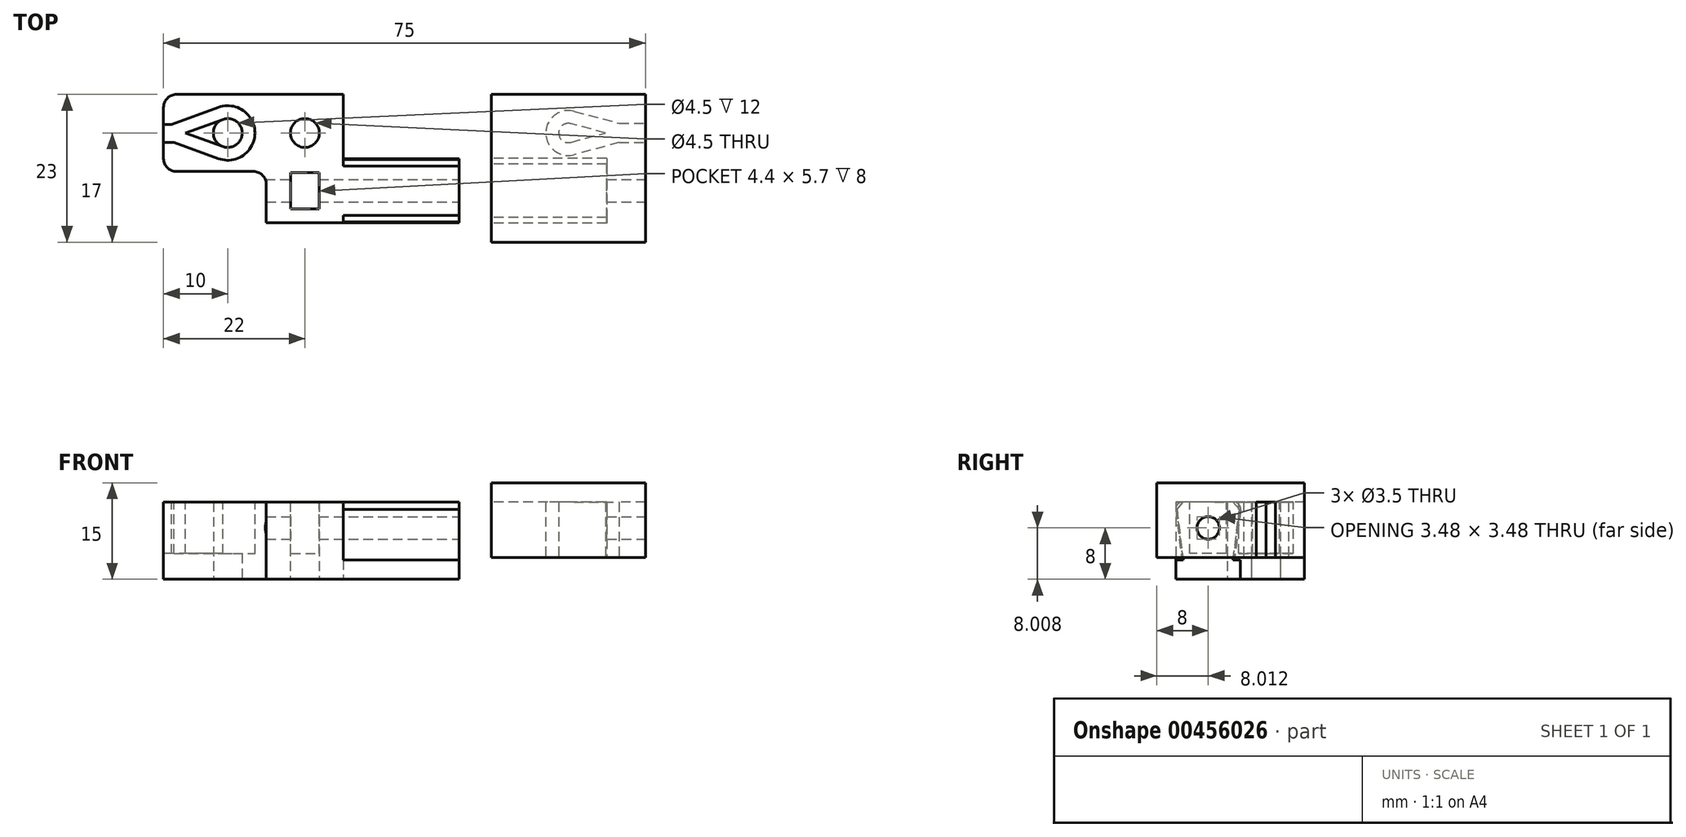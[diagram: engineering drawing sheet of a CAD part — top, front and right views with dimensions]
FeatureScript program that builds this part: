
annotation { "Feature Type Name" : "Feature", "Feature Type Description" : "" }
export const myFeature = defineFeature(function(context is Context, id is Id, definition is map)
    precondition{}
    {
        {
            var Q0;
            Q0=qCreatedBy(makeId("Top.planeOp"),FACE);
            var sketch = newSketch(context, id + "F0", { "sketchPlane" : qUnion([Q0])});
            skLineSegment(sketch, "E0.bottom", {"start": v(-8, -6) * mm, "end": v(4, -6) * mm});
            skLineSegment(sketch, "E0.top", {"start": v(-8, 6) * mm, "end": v(18, 6) * mm});
            skLineSegment(sketch, "E0.left", {"start": v(-10, -4) * mm, "end": v(-10, 4) * mm});
            skLineSegment(sketch, "E0.right", {"start": v(36, -6) * mm, "end": v(36, -4) * mm});
            skCircle(sketch, "E1", {"center": v(0, 0) * mm, "radius": 2.25 * mm, "construction": true});
            skPoint(sketch, "E2.visualSharp", {"position": v(-10, 6) * mm});
            skArc(sketch, "E2.filletArc", {"start": v(-8, 6) * mm, "mid": v(-9.41, 5.41) * mm, "end": v(-10, 4) * mm});
            skPoint(sketch, "E3.visualSharp", {"position": v(-10, -6) * mm});
            skArc(sketch, "E3.filletArc", {"start": v(-10, -4) * mm, "mid": v(-9.41, -5.41) * mm, "end": v(-8, -6) * mm});
            skCircle(sketch, "E4", {"center": v(12, 0) * mm, "radius": 2.25 * mm, "construction": true});
            skLineSegment(sketch, "E5", {"start": v(6, -8) * mm, "end": v(6, -14) * mm});
            skLineSegment(sketch, "E6", {"start": v(6, -14) * mm, "end": v(36, -14) * mm});
            skLineSegment(sketch, "E7", {"start": v(36, -6) * mm, "end": v(36, -14) * mm});
            skPoint(sketch, "E8.visualSharp", {"position": v(6, -6) * mm});
            skArc(sketch, "E8.filletArc", {"start": v(6, -8) * mm, "mid": v(5.41, -6.59) * mm, "end": v(4, -6) * mm});
            skLineSegment(sketch, "E9", {"start": v(18, 6) * mm, "end": v(18, -4) * mm});
            skLineSegment(sketch, "E10", {"start": v(18, -4) * mm, "end": v(36, -4) * mm});
            skSolve(sketch);
        }
        {
            var Q0;
            Q0 = qSketchRegion(id + "F0", true);
            extrude(context, id + "F1", {"entities" : qUnion([Q0]), "depth" : 12 * mm});
        }
        {
            var Q0;
            Q0=makeQuery(id+"F1.opExtrude","SWEPT_FACE",FACE,{"disambiguationData":[OSD([sQuery(id+"F0.wireOp",EDGE,"E0.right"),sQuery(id+"F0.wireOp",EDGE,"E7")])]});
            var sketch = newSketch(context, id + "F2", { "sketchPlane" : qUnion([Q0])});
            skLineSegment(sketch, "E11", {"start": v(-14, 12) * mm, "end": v(-12.9, 3) * mm});
            skLineSegment(sketch, "E12", {"start": v(-12.9, 3) * mm, "end": v(-16, 3) * mm});
            skLineSegment(sketch, "E13", {"start": v(-16, 3) * mm, "end": v(-16, 12) * mm});
            skLineSegment(sketch, "E14", {"start": v(-16, 12) * mm, "end": v(-14, 12) * mm});
            skPoint(sketch, "E15", {"position": v(-9, 0) * mm});
            skLineSegment(sketch, "E16", {"start": v(-9, -1.64) * mm, "end": v(-9, 13.82) * mm, "construction": true});
            skLineSegment(sketch, "E17.MirrorCS", {"start": v(-2, 12) * mm, "end": v(-4, 12) * mm});
            skLineSegment(sketch, "E18.MirrorCS", {"start": v(-2, 3) * mm, "end": v(-2, 12) * mm});
            skLineSegment(sketch, "E19.MirrorCS", {"start": v(-4, 12) * mm, "end": v(-5.1, 3) * mm});
            skLineSegment(sketch, "E20.MirrorCS", {"start": v(-5.1, 3) * mm, "end": v(-2, 3) * mm});
            skSolve(sketch);
        }
        {
            var Q0;
            Q0 = qSketchRegion(id + "F2", true);
            var Q1;
            Q1=makeQuery(id+"F1.opExtrude","SWEPT_FACE",FACE,{"disambiguationData":[OSD([sQuery(id+"F0.wireOp",EDGE,"E9")])]});
            extrude(context, id + "F3", {"entities" : qUnion([Q0]), "operationType" : NewBodyOperationType.REMOVE, "endBound" : BoundingType.UP_TO_SURFACE, "oppositeDirection" : true, "endBoundEntityFace" : qUnion([Q1]), "depth" : 25 * mm});
        }
        {
            var Q0;
            {var subQ0=sQuery(id+"F0.wireOp",EDGE,"E6");Q0=makeQuery(id+"F3.boolean.opBoolean","MERGE",EDGE,{"derivedFrom":[makeQuery(id+"F1.opExtrude","CAP_EDGE",EDGE,{"disambiguationData":[OSD([subQ0])],"isStart":false}),makeQuery(id+"F3.opExtrude","SWEPT_EDGE",EDGE,{"disambiguationData":[OSD([sQuery(id+"F0.wireOp",EDGE,"E0.right"),subQ0,sQuery(id+"F0.wireOp",EDGE,"E7"),sQuery(id+"F2.wireOp",EDGE,"E11"),sQuery(id+"F2.wireOp",EDGE,"E14")])]})]});}
            var Q1;
            {var subQ0=sQuery(id+"F0.wireOp",EDGE,"E10");Q1=makeQuery(id+"F3.boolean.opBoolean","MERGE",EDGE,{"derivedFrom":[makeQuery(id+"F1.opExtrude","CAP_EDGE",EDGE,{"disambiguationData":[OSD([subQ0])],"isStart":false}),makeQuery(id+"F3.opExtrude","SWEPT_EDGE",EDGE,{"disambiguationData":[OSD([sQuery(id+"F0.wireOp",EDGE,"E0.right"),sQuery(id+"F0.wireOp",EDGE,"E7"),subQ0,sQuery(id+"F2.wireOp",EDGE,"E17.MirrorCS"),sQuery(id+"F2.wireOp",EDGE,"E19.MirrorCS")])]})]});}
            chamfer(context, id + "F4", {"entities" : qUnion([Q0, Q1]), "width" : 1 * mm});
        }
        {
            var Q0;
            Q0=sQuery(id+"F0.wireOp",VERTEX,"E1.center");
            var Q1;
            Q1=sQuery(id+"F0.wireOp",VERTEX,"E4.center");
            var Q2;
            Q2=makeQuery(id+"F1.opExtrude","SWEPT_BODY",BODY,{"disambiguationData":[OSD([sQuery(id+"F0.wireOp",EDGE,"E0.bottom"),sQuery(id+"F0.wireOp",EDGE,"E0.top"),sQuery(id+"F0.wireOp",EDGE,"E0.left"),sQuery(id+"F0.wireOp",EDGE,"E0.right"),sQuery(id+"F0.wireOp",EDGE,"E2.filletArc"),sQuery(id+"F0.wireOp",EDGE,"E3.filletArc"),sQuery(id+"F0.wireOp",EDGE,"E5"),sQuery(id+"F0.wireOp",EDGE,"E6"),sQuery(id+"F0.wireOp",EDGE,"E7"),sQuery(id+"F0.wireOp",EDGE,"E8.filletArc"),sQuery(id+"F0.wireOp",EDGE,"E9"),sQuery(id+"F0.wireOp",EDGE,"E10")])]});
            hole(context, id + "F5", {"style" : HoleStyle.SIMPLE, "endStyle" : HoleEndStyle.THROUGH, "oppositeDirection" : true, "holeDiameter" : 4.5 * mm, "isTappedThrough" : true, "tappedDepth" : 12 * mm, "tapClearance" : 3, "startFromSketch" : true, "locations" : qUnion([Q0, Q1]), "scope" : qUnion([Q2])});
        }
        {
            var Q0;
            Q0=makeQuery(id+"F1.opExtrude","SWEPT_FACE",FACE,{"disambiguationData":[OSD([sQuery(id+"F0.wireOp",EDGE,"E0.right"),sQuery(id+"F0.wireOp",EDGE,"E7")])]});
            var sketch = newSketch(context, id + "F6", { "sketchPlane" : qUnion([Q0])});
            skPoint(sketch, "E21", {"position": v(-9, 0) * mm});
            skLineSegment(sketch, "E22", {"start": v(-9, -0.78) * mm, "end": v(-9, 13.1) * mm, "construction": true});
            skCircle(sketch, "E23", {"center": v(-9, 8) * mm, "radius": 1.75 * mm});
            skSolve(sketch);
        }
        {
            var Q0;
            Q0 = qSketchRegion(id + "F6", true);
            extrude(context, id + "F7", {"entities" : qUnion([Q0]), "operationType" : NewBodyOperationType.REMOVE, "oppositeDirection" : true, "depth" : 35 * mm});
        }
        {
            var Q0;
            Q0=makeQuery(id+"F1.opExtrude","CAP_FACE",FACE,{"disambiguationData":[OSD([sQuery(id+"F0.wireOp",EDGE,"E0.bottom"),sQuery(id+"F0.wireOp",EDGE,"E0.top"),sQuery(id+"F0.wireOp",EDGE,"E0.left"),sQuery(id+"F0.wireOp",EDGE,"E0.right"),sQuery(id+"F0.wireOp",EDGE,"E2.filletArc"),sQuery(id+"F0.wireOp",EDGE,"E3.filletArc"),sQuery(id+"F0.wireOp",EDGE,"E5"),sQuery(id+"F0.wireOp",EDGE,"E6"),sQuery(id+"F0.wireOp",EDGE,"E7"),sQuery(id+"F0.wireOp",EDGE,"E8.filletArc"),sQuery(id+"F0.wireOp",EDGE,"E9"),sQuery(id+"F0.wireOp",EDGE,"E10")])],"isStart":false});
            var sketch = newSketch(context, id + "F8", { "sketchPlane" : qUnion([Q0])});
            skLineSegment(sketch, "E24.bottom", {"start": v(9.8, -6.15) * mm, "end": v(14.2, -6.15) * mm});
            skLineSegment(sketch, "E24.top", {"start": v(9.8, -11.85) * mm, "end": v(14.2, -11.85) * mm});
            skLineSegment(sketch, "E24.left", {"start": v(9.8, -6.15) * mm, "end": v(9.8, -11.85) * mm});
            skLineSegment(sketch, "E24.right", {"start": v(14.2, -6.15) * mm, "end": v(14.2, -11.85) * mm});
            skPoint(sketch, "E25", {"position": v(14.2, -9) * mm});
            skPoint(sketch, "E26", {"position": v(12, -6.15) * mm});
            skLineSegment(sketch, "E27", {"start": v(12, 0) * mm, "end": v(12, -15.07) * mm, "construction": true});
            skPoint(sketch, "E28", {"position": v(36, -9) * mm});
            skLineSegment(sketch, "E29", {"start": v(36, -9) * mm, "end": v(2.23, -9) * mm, "construction": true});
            skSolve(sketch);
        }
        {
            var Q0;
            Q0 = qSketchRegion(id + "F8", true);
            extrude(context, id + "F9", {"entities" : qUnion([Q0]), "operationType" : NewBodyOperationType.REMOVE, "oppositeDirection" : true, "depth" : 8 * mm});
        }
        {
            var Q0;
            Q0=makeQuery(id+"F1.opExtrude","CAP_FACE",FACE,{"disambiguationData":[OSD([sQuery(id+"F0.wireOp",EDGE,"E0.bottom"),sQuery(id+"F0.wireOp",EDGE,"E0.top"),sQuery(id+"F0.wireOp",EDGE,"E0.left"),sQuery(id+"F0.wireOp",EDGE,"E0.right"),sQuery(id+"F0.wireOp",EDGE,"E2.filletArc"),sQuery(id+"F0.wireOp",EDGE,"E3.filletArc"),sQuery(id+"F0.wireOp",EDGE,"E5"),sQuery(id+"F0.wireOp",EDGE,"E6"),sQuery(id+"F0.wireOp",EDGE,"E7"),sQuery(id+"F0.wireOp",EDGE,"E8.filletArc"),sQuery(id+"F0.wireOp",EDGE,"E9"),sQuery(id+"F0.wireOp",EDGE,"E10")])],"isStart":false});
            var sketch = newSketch(context, id + "F10", { "sketchPlane" : qUnion([Q0])});
            skLineSegment(sketch, "E30", {"start": v(-0.77, 2.11) * mm, "end": v(-6.58, 0) * mm});
            skLineSegment(sketch, "E31", {"start": v(-6.58, 0) * mm, "end": v(-0.77, -2.11) * mm});
            skArc(sketch, "E32.0", {"start": v(-0.77, -2.11) * mm, "mid": v(2.25, 0) * mm, "end": v(-0.77, 2.11) * mm});
            skLineSegment(sketch, "E33", {"start": v(0, 0) * mm, "end": v(-11.05, 0) * mm, "construction": true});
            skPoint(sketch, "E33.endSnap0", {"position": v(-10, 0) * mm});
            skLineSegment(sketch, "E34.0", {"start": v(-8.4, -1.47) * mm, "end": v(-1.47, -3.99) * mm});
            skLineSegment(sketch, "E35.0", {"start": v(-1.47, 3.99) * mm, "end": v(-8.76, 1.33) * mm});
            skLineSegment(sketch, "E36", {"start": v(-10.71, 1.33) * mm, "end": v(-10.71, -1.47) * mm});
            skLineSegment(sketch, "E37.trimOffspring", {"start": v(-8.76, 1.33) * mm, "end": v(-10.71, 1.33) * mm});
            skLineSegment(sketch, "E38.trimOffspring", {"start": v(-8.4, -1.47) * mm, "end": v(-10.71, -1.47) * mm});
            skArc(sketch, "E39.trimOffspring", {"start": v(-1.47, -3.99) * mm, "mid": v(4.23, 0) * mm, "end": v(-1.47, 3.99) * mm});
            skSolve(sketch);
        }
        {
            var Q0;
            Q0 = qSketchRegion(id + "F10", true);
            extrude(context, id + "F11", {"entities" : qUnion([Q0]), "operationType" : NewBodyOperationType.REMOVE, "oppositeDirection" : true, "depth" : 8 * mm});
        }
        {
            var Q0;
            Q0=makeQuery(id+"F6.imprint","IMPRINT",FACE,{"disambiguationData":[TD([[makeQuery(id+"F6.imprint","IMPRINT",EDGE,{"derivedFrom":sQuery(id+"F6.wireOp",EDGE,"E23")}),-1.0]])]});
            cPlane(context, id + "F12", {"entities" : qUnion([Q0]), "cplaneType" : CPlaneType.OFFSET, "offset" : 5 * mm, "width" : 150 * mm, "height" : 150 * mm});
        }
        {
            var Q0;
            Q0=qCreatedBy(id+"F12.planeOp",FACE);
            var sketch = newSketch(context, id + "F13", { "sketchPlane" : qUnion([Q0])});
            skLineSegment(sketch, "E40.0", {"start": v(-14.06, 10.8) * mm, "end": v(-13.15, 3.4) * mm});
            skLineSegment(sketch, "E41.0", {"start": v(-3.94, 10.8) * mm, "end": v(-4.85, 3.4) * mm});
            skLineSegment(sketch, "E42.0", {"start": v(-13.15, 3.4) * mm, "end": v(-14, 3.4) * mm});
            skLineSegment(sketch, "E43.0", {"start": v(-4.85, 3.4) * mm, "end": v(-4, 3.4) * mm});
            skLineSegment(sketch, "E44", {"start": v(-14, 3.4) * mm, "end": v(-17, 3.4) * mm});
            skLineSegment(sketch, "E45", {"start": v(-17, 3.4) * mm, "end": v(-17, 15) * mm});
            skLineSegment(sketch, "E46", {"start": v(-17, 15) * mm, "end": v(6, 15) * mm});
            skLineSegment(sketch, "E47", {"start": v(6, 15) * mm, "end": v(6, 3.4) * mm});
            skLineSegment(sketch, "E48", {"start": v(6, 3.4) * mm, "end": v(-4, 3.4) * mm});
            skLineSegment(sketch, "E49.0", {"start": v(-5, 12) * mm, "end": v(-13, 12) * mm});
            skArc(sketch, "E50", {"start": v(-13, 12) * mm, "mid": v(-13.8, 11.64) * mm, "end": v(-14.06, 10.8) * mm});
            skArc(sketch, "E51", {"start": v(-3.94, 10.8) * mm, "mid": v(-4.2, 11.64) * mm, "end": v(-5, 12) * mm});
            skPoint(sketch, "E52.orphan", {"position": v(-13, 12) * mm});
            skPoint(sketch, "E53.orphan", {"position": v(-5, 12) * mm});
            skSolve(sketch);
        }
        {
            var Q0;
            Q0 = qSketchRegion(id + "F13", true);
            extrude(context, id + "F14", {"entities" : qUnion([Q0]), "depth" : 24 * mm});
        }
        {
            var Q0;
            Q0=makeQuery(id+"F14.opExtrude","CAP_FACE",FACE,{"disambiguationData":[OSD([sQuery(id+"F13.wireOp",EDGE,"E40.0"),sQuery(id+"F13.wireOp",EDGE,"E41.0"),sQuery(id+"F13.wireOp",EDGE,"E42.0"),sQuery(id+"F13.wireOp",EDGE,"E43.0"),sQuery(id+"F13.wireOp",EDGE,"E44"),sQuery(id+"F13.wireOp",EDGE,"E45"),sQuery(id+"F13.wireOp",EDGE,"E46"),sQuery(id+"F13.wireOp",EDGE,"E47"),sQuery(id+"F13.wireOp",EDGE,"E48"),sQuery(id+"F13.wireOp",EDGE,"E49.0"),sQuery(id+"F13.wireOp",EDGE,"E50"),sQuery(id+"F13.wireOp",EDGE,"E51")])],"isStart":false});
            var sketch = newSketch(context, id + "F15", { "sketchPlane" : qUnion([Q0])});
            skLineSegment(sketch, "E54.bottom", {"start": v(-17, 15) * mm, "end": v(-3, 15) * mm});
            skLineSegment(sketch, "E54.top", {"start": v(-17, 3.4) * mm, "end": v(-3, 3.4) * mm});
            skLineSegment(sketch, "E54.left", {"start": v(-17, 15) * mm, "end": v(-17, 3.4) * mm});
            skLineSegment(sketch, "E54.right", {"start": v(-3, 15) * mm, "end": v(-3, 3.4) * mm});
            skSolve(sketch);
        }
        {
            var Q0;
            Q0 = qSketchRegion(id + "F15", true);
            extrude(context, id + "F16", {"entities" : qUnion([Q0]), "operationType" : NewBodyOperationType.ADD, "oppositeDirection" : true, "depth" : 6 * mm});
        }
        {
            var Q0;
            Q0=makeQuery(id+"F16.boolean.opBoolean","MERGE",FACE,{"derivedFrom":[makeQuery(id+"F14.opExtrude","CAP_FACE",FACE,{"disambiguationData":[OSD([sQuery(id+"F13.wireOp",EDGE,"E40.0"),sQuery(id+"F13.wireOp",EDGE,"E41.0"),sQuery(id+"F13.wireOp",EDGE,"E42.0"),sQuery(id+"F13.wireOp",EDGE,"E43.0"),sQuery(id+"F13.wireOp",EDGE,"E44"),sQuery(id+"F13.wireOp",EDGE,"E45"),sQuery(id+"F13.wireOp",EDGE,"E46"),sQuery(id+"F13.wireOp",EDGE,"E47"),sQuery(id+"F13.wireOp",EDGE,"E48"),sQuery(id+"F13.wireOp",EDGE,"E49.0"),sQuery(id+"F13.wireOp",EDGE,"E50"),sQuery(id+"F13.wireOp",EDGE,"E51")])],"isStart":false}),makeQuery(id+"F16.opExtrude","CAP_FACE",FACE,{"disambiguationData":[OSD([sQuery(id+"F15.wireOp",EDGE,"E54.bottom"),sQuery(id+"F15.wireOp",EDGE,"E54.top"),sQuery(id+"F15.wireOp",EDGE,"E54.left"),sQuery(id+"F15.wireOp",EDGE,"E54.right")])],"isStart":true})]});
            var sketch = newSketch(context, id + "F17", { "sketchPlane" : qUnion([Q0])});
            skCircle(sketch, "E55.0", {"center": v(-9, 8) * mm, "radius": 1.75 * mm});
            skSolve(sketch);
        }
        {
            var Q0;
            Q0 = qSketchRegion(id + "F17", true);
            var Q1;
            Q1=makeQuery(id+"F16.opExtrude","CAP_FACE",FACE,{"disambiguationData":[OSD([sQuery(id+"F15.wireOp",EDGE,"E54.bottom"),sQuery(id+"F15.wireOp",EDGE,"E54.top"),sQuery(id+"F15.wireOp",EDGE,"E54.left"),sQuery(id+"F15.wireOp",EDGE,"E54.right")])],"isStart":false});
            extrude(context, id + "F18", {"entities" : qUnion([Q0]), "operationType" : NewBodyOperationType.REMOVE, "endBound" : BoundingType.UP_TO_SURFACE, "oppositeDirection" : true, "endBoundEntityFace" : qUnion([Q1]), "depth" : 25 * mm});
        }
        {
            var Q0;
            Q0=makeQuery(id+"F16.boolean.opBoolean","MERGE",FACE,{"derivedFrom":[makeQuery(id+"F14.opExtrude","SWEPT_FACE",FACE,{"disambiguationData":[OSD([sQuery(id+"F13.wireOp",EDGE,"E42.0"),sQuery(id+"F13.wireOp",EDGE,"E44")])]}),makeQuery(id+"F14.opExtrude","SWEPT_FACE",FACE,{"disambiguationData":[OSD([sQuery(id+"F13.wireOp",EDGE,"E43.0"),sQuery(id+"F13.wireOp",EDGE,"E48")])]}),makeQuery(id+"F16.opExtrude","SWEPT_FACE",FACE,{"disambiguationData":[OSD([sQuery(id+"F15.wireOp",EDGE,"E54.top")])]})]});
            var sketch = newSketch(context, id + "F19", { "sketchPlane" : qUnion([Q0])});
            skArc(sketch, "E56", {"start": v(53.39, 1.45) * mm, "mid": v(51.5, 0) * mm, "end": v(53.39, -1.45) * mm});
            skLineSegment(sketch, "E57", {"start": v(53.39, -1.45) * mm, "end": v(58.8, 0) * mm});
            skLineSegment(sketch, "E58", {"start": v(58.8, 0) * mm, "end": v(53.39, 1.45) * mm});
            skArc(sketch, "E59.0", {"start": v(53.9, 3.38) * mm, "mid": v(49.5, 0) * mm, "end": v(53.9, -3.38) * mm});
            skLineSegment(sketch, "E60.0", {"start": v(60.92, 1.5) * mm, "end": v(53.9, 3.38) * mm});
            skLineSegment(sketch, "E61.0", {"start": v(53.9, -3.38) * mm, "end": v(60.92, -1.5) * mm});
            skLineSegment(sketch, "E62", {"start": v(53, 0) * mm, "end": v(66.25, 0) * mm, "construction": true});
            skLineSegment(sketch, "E63.0", {"start": v(60.92, -1.5) * mm, "end": v(66, -1.5) * mm});
            skLineSegment(sketch, "E64.0", {"start": v(60.92, 1.5) * mm, "end": v(66, 1.5) * mm});
            skLineSegment(sketch, "E65", {"start": v(66, -1.5) * mm, "end": v(66, 1.5) * mm});
            skSolve(sketch);
        }
        {
            var Q0;
            Q0 = qSketchRegion(id + "F19", true);
            var Q1;
            Q1=makeQuery(id+"F14.opExtrude","SWEPT_FACE",FACE,{"disambiguationData":[OSD([sQuery(id+"F13.wireOp",EDGE,"E49.0")])]});
            extrude(context, id + "F20", {"entities" : qUnion([Q0]), "operationType" : NewBodyOperationType.REMOVE, "endBound" : BoundingType.UP_TO_SURFACE, "oppositeDirection" : true, "endBoundEntityFace" : qUnion([Q1]), "depth" : 25 * mm});
        }
    });
